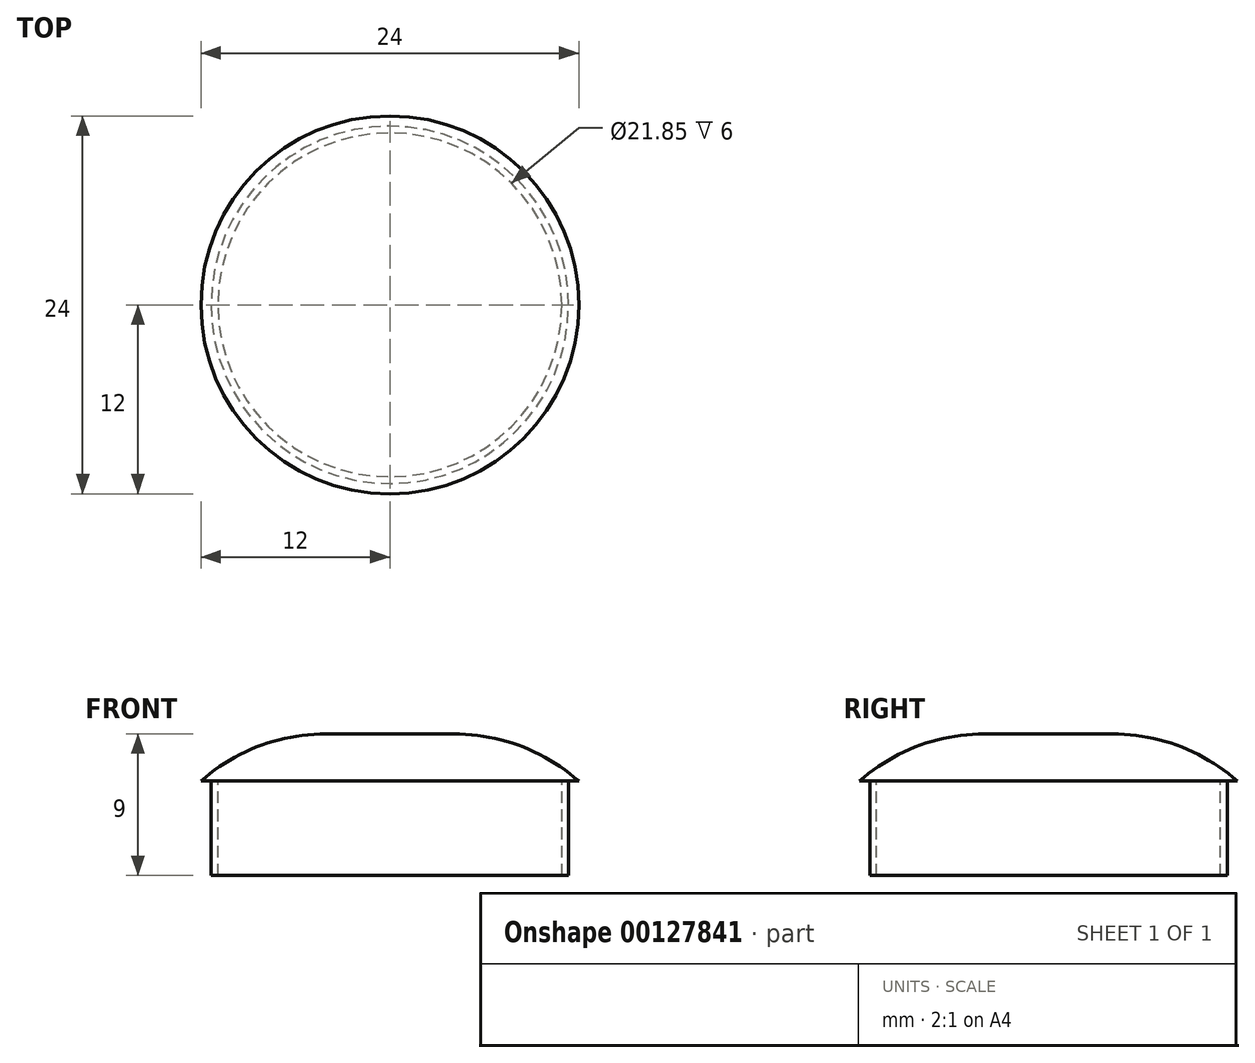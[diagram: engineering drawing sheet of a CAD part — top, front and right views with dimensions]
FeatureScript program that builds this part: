
annotation { "Feature Type Name" : "Feature", "Feature Type Description" : "" }
export const myFeature = defineFeature(function(context is Context, id is Id, definition is map)
    precondition{}
    {
        {
            var Q0;
            Q0=qCreatedBy(makeId("Top.planeOp"),FACE);
            var sketch = newSketch(context, id + "F0", { "sketchPlane" : qUnion([Q0])});
            skCircle(sketch, "E0", {"center": v(0, 0) * mm, "radius": 11.35 * mm});
            skCircle(sketch, "E1", {"center": v(0, 0) * mm, "radius": 12 * mm});
            skCircle(sketch, "E2", {"center": v(0, 0) * mm, "radius": 10.92 * mm});
            skSolve(sketch);
        }
        {
            var Q0;
            Q0=makeQuery(id+"F0.imprint","IMPRINT",FACE,{"disambiguationData":[TD([[makeQuery(id+"F0.imprint","IMPRINT",EDGE,{"derivedFrom":sQuery(id+"F0.wireOp",EDGE,"E0")}),1.0]])]});
            extrude(context, id + "F1", {"entities" : qUnion([Q0]), "oppositeDirection" : true, "depth" : 6 * mm});
        }
        {
            var Q0;
            Q0=makeQuery(id+"F0.imprint","IMPRINT",FACE,{"disambiguationData":[TD([[makeQuery(id+"F0.imprint","IMPRINT",EDGE,{"derivedFrom":sQuery(id+"F0.wireOp",EDGE,"E2")}),1.0]])]});
            var Q1;
            Q1=makeQuery(id+"F0.imprint","IMPRINT",FACE,{"disambiguationData":[TD([[makeQuery(id+"F0.imprint","IMPRINT",EDGE,{"derivedFrom":sQuery(id+"F0.wireOp",EDGE,"E0")}),-1.0]])]});
            var Q2;
            Q2=makeQuery(id+"F0.imprint","IMPRINT",FACE,{"disambiguationData":[TD([[makeQuery(id+"F0.imprint","IMPRINT",EDGE,{"derivedFrom":sQuery(id+"F0.wireOp",EDGE,"E0")}),1.0]])]});
            extrude(context, id + "F2", {"entities" : qUnion([Q0, Q1, Q2]), "operationType" : NewBodyOperationType.ADD, "depth" : 3 * mm});
        }
        {
            var Q0;
            Q0=makeQuery(id+"F2.opExtrude","CAP_FACE",FACE,{"disambiguationData":[OSD([sQuery(id+"F0.wireOp",EDGE,"E1")])],"isStart":false});
            fillet(context, id + "F3", {"entities" : qUnion([Q0]), "radius" : 12 * mm, "tangentPropagation" : true, "allowEdgeOverflow" : false});
        }
    });
